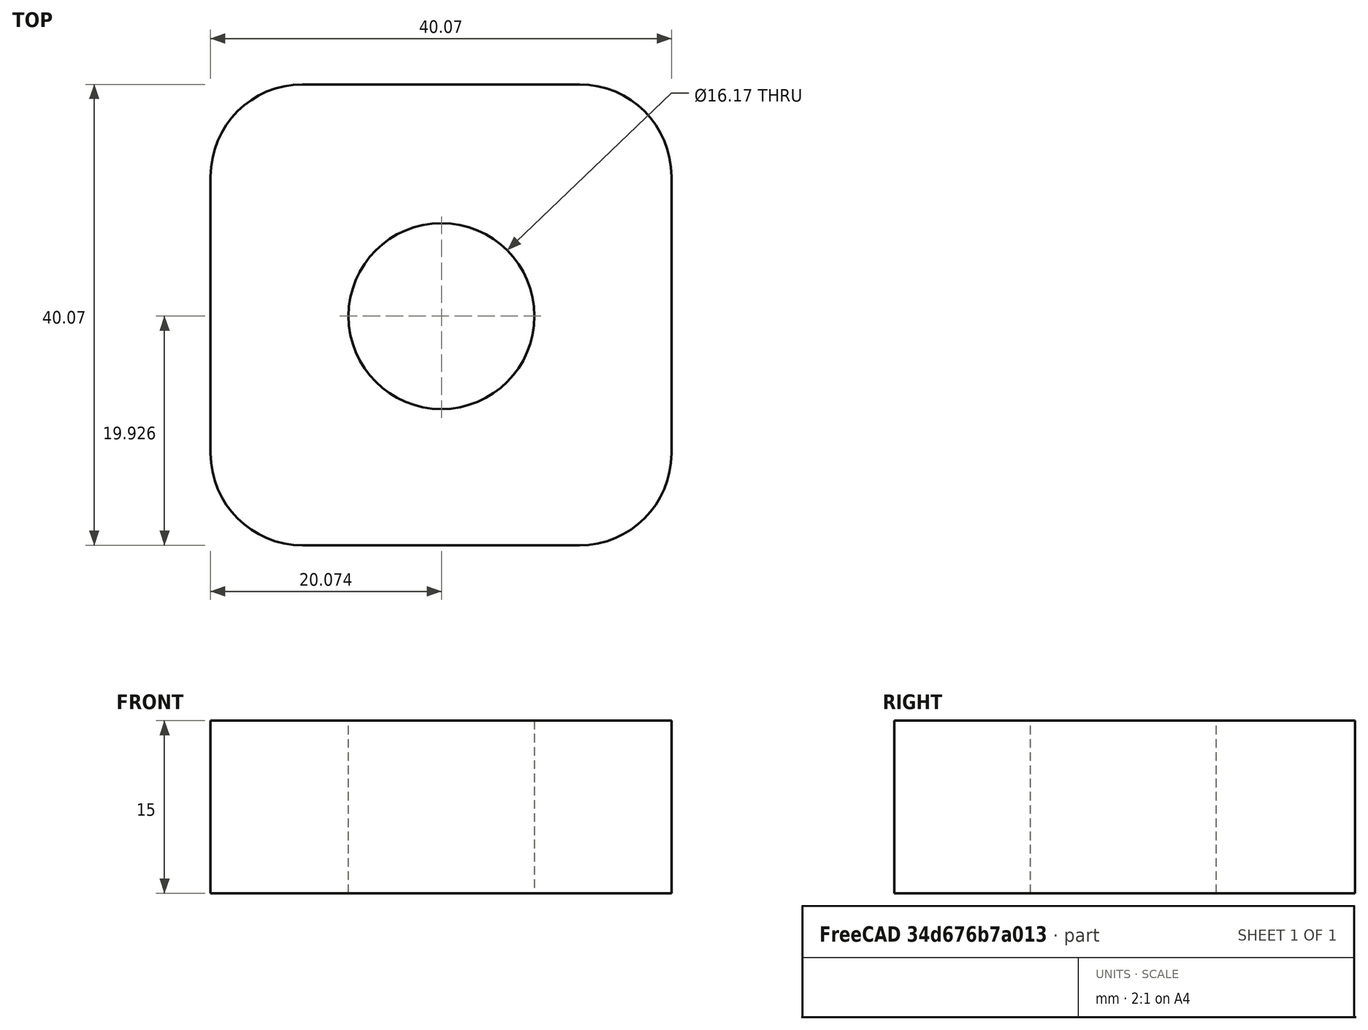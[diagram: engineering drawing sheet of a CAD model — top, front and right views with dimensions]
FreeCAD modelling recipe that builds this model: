
FCSTD DOCUMENT  (FreeCAD 0.21R32552 (Git))
Label: 8x
License: All rights reserved
LicenseURL: http://en.wikipedia.org/wiki/All_rights_reserved
objects: App::FeaturePython×9, App::DocumentObjectGroupPython×4, TechDraw::DrawProjGroupItem×3, TechDraw::DrawViewBalloon×3, Sketcher::SketchObject×2, PartDesign::Pad×1, PartDesign::Pocket×1, PartDesign::Fillet×1, PartDesign::Body×1, TechDraw::DrawSVGTemplate×1, TechDraw::DrawProjGroup×1, TechDraw::DrawPage×1
note: 9 computed .brp shape members not serialized (recipe doc carries the construction recipe); baked Part::Feature solids carry a one-line shape summary decoded from their .brp

FEATURE [Sketcher::SketchObject] Sketch
  FullyConstrained = false
  MapMode = 5
  Support = -> [XY_Plane]
  sketch-geometry (4):
    g0: LineSegment StartX=0 StartY=0 StartZ=0 EndX=40.0741 EndY=0 EndZ=0
    g1: LineSegment StartX=40.0741 StartY=0 StartZ=0 EndX=40.0741 EndY=40.0741 EndZ=0
    g2: LineSegment StartX=40.0741 StartY=40.0741 StartZ=0 EndX=0 EndY=40.0741 EndZ=0
    g3: LineSegment StartX=0 StartY=40.0741 StartZ=0 EndX=0 EndY=0 EndZ=0
  constraints (9):
    c: Coincident(g0,g1)
    c: Coincident(g1,g2)
    c: Coincident(g2,g3)
    c: Coincident(g3,g0)
    c: Horizontal(g0)
    c: Horizontal(g2)
    c: Vertical(g1)
    c: Vertical(g3)
    c: Coincident(g0,g-1)
FEATURE [PartDesign::Pad] Pad
  Direction = (0,0,1)
  Length = 15
  Length2 = 10
  Profile = -> Sketch
  ReferenceAxis = -> Sketch [N_Axis]
  Type = 0
FEATURE [Sketcher::SketchObject] Sketch001
  FullyConstrained = false
  MapMode = 5
  Placement = pos=(0,0,15) rot=(0,0,1;0rad)
  Support = -> [Pad]
  sketch-geometry (1):
    g0: Circle CenterX=20.0741 CenterY=19.9259 CenterZ=0 NormalX=0 NormalY=0 NormalZ=1 AngleXU=0 Radius=8.08325
FEATURE [PartDesign::Pocket] Pocket
  BaseFeature = -> Pad
  Direction = (0,0,-1)
  Length = 5
  Length2 = 5
  Profile = -> Sketch001
  ReferenceAxis = -> Sketch001 [N_Axis]
  Type = 1
FEATURE [PartDesign::Fillet] Fillet
  Base = -> Pocket [Edge2,Edge8,Edge5,Edge1]
  BaseFeature = -> Pocket
  Radius = 8
  SupportTransform = false
  UseAllEdges = false
FEATURE [PartDesign::Body] Body
  Group = -> [Sketch,Pad,Sketch001,Pocket,Fillet]
  Origin = -> Origin
  Tip = -> Fillet
FEATURE [App::FeaturePython] AnnotationPlane  label="AP1"  # WARN: FeaturePython — macro-defined, semantics opaque (R4)
  Direction = (0,1,0)
  Offset = -10
  PointWithOffset = (20.037,30.0741,7.5)
  Type = Unknown
  faces = -> Fillet [Face10]
  p1 = (20.037,40.0741,7.5)
FEATURE [App::FeaturePython] DatumFeature  label="A"  # WARN: FeaturePython — macro-defined, semantics opaque (R4)
  Type = Unknown
FEATURE [App::FeaturePython] DatumSystem  label="DS1: A"  # WARN: FeaturePython — macro-defined, semantics opaque (R4)
  Primary = -> DatumFeature
  Type = Unknown
FEATURE [App::FeaturePython] DatumFeature001  label="B"  # WARN: FeaturePython — macro-defined, semantics opaque (R4)
  Type = Unknown
FEATURE [App::DocumentObjectGroupPython] Annotation2  # scripted group (container) (typed FeaturePython)
  AP = -> AnnotationPlane
  DF = -> DatumFeature001
  Direction = (0,1,0)
  Group = -> [DatumFeature001]
  circumferenceBool = true
  diameter = 0
  faces = -> [Fillet]
  highLimit = 0
  lowLimit = 0
  p1 = (28.1573,19.9259,15)
  selectedPoint = (31.0176,29.9998,17.166)
  spBool = true
  toleranceDiameter = 0
  toleranceSelectBool = true
FEATURE [App::FeaturePython] DatumSystem001  label="DS2: B"  # WARN: FeaturePython — macro-defined, semantics opaque (R4)
  Primary = -> DatumFeature001
  Type = Unknown
FEATURE [App::FeaturePython] AnnotationPlane001  label="AP2"  # WARN: FeaturePython — macro-defined, semantics opaque (R4)
  Direction = (0,0,1)
  Offset = -5
  PointWithOffset = (20.0314,20.054,10)
  Type = Unknown
  faces = -> Fillet [Face5]
  p1 = (20.0314,20.054,15)
FEATURE [App::FeaturePython] GeometricTolerance  label="GT1"  # WARN: FeaturePython — macro-defined, semantics opaque (R4)
  Characteristic = Profile of a surface
  CharacteristicCode = ⌓
  CharacteristicIcon = :/dd/icons/Characteristic/profileOfASurface.svg
  Circumference = false
  DS = -> DatumSystem001
  FeatureControlFrame = Maximum material condition
  FeatureControlFrameCode = Ⓜ
  FeatureControlFrameIcon = :/dd/icons/FeatureControlFrame/maximumMaterialCondition.svg
  ToleranceValue = 0.3
  Type = Unknown
FEATURE [App::DocumentObjectGroupPython] Annotation3  # scripted group (container) (typed FeaturePython)
  AP = -> AnnotationPlane001
  Direction = (0,-1,0)
  GT = -> [GeometricTolerance]
  circumferenceBool = false
  diameter = 0
  faces = -> [Fillet]
  highLimit = 0
  lowLimit = 0
  p1 = (20.037,0,10)
  selectedPoint = (9.03139,-13.946,10)
  spBool = true
  toleranceDiameter = 0
  toleranceSelectBool = true
FEATURE [App::FeaturePython] AnnotationPlane002  label="AP3"  # WARN: FeaturePython — macro-defined, semantics opaque (R4)
  Direction = (0,1,0)
  PointWithOffset = (20.037,40.0741,7.5)
  Type = Unknown
  faces = -> Fillet [Face10]
  p1 = (20.037,40.0741,7.5)
FEATURE [App::FeaturePython] AnnotationPlane003  label="AP4"  # WARN: FeaturePython — macro-defined, semantics opaque (R4)
  Direction = (0,-1,0)
  Offset = -20
  PointWithOffset = (20.037,20,7.5)
  Type = Unknown
  faces = -> Fillet [Face1]
  p1 = (20.037,0,7.5)
FEATURE [App::DocumentObjectGroupPython] Annotation1  # scripted group (container) (typed FeaturePython)
  AP = -> AnnotationPlane003
  DF = -> DatumFeature
  Direction = (0,0,-1)
  Group = -> [DatumFeature]
  circumferenceBool = false
  diameter = 0
  faces = -> [Fillet]
  highLimit = 0
  lowLimit = 0
  p1 = (20.0314,20,0)
  selectedPoint = (22.1323,10.2224,-9.5)
  spBool = true
  toleranceDiameter = 0
  toleranceSelectBool = true
FEATURE [App::DocumentObjectGroupPython] GDT  # scripted group (container) (typed FeaturePython)
  Group = -> [Annotation1,DatumSystem,Annotation2,DatumSystem001,Annotation3,AnnotationPlane002,AnnotationPlane003]
  Type = Unknown
FEATURE [TechDraw::DrawSVGTemplate] Template
  Height = 297
  Orientation = 1
  Template = <path> 0.21/data/Mod/TechDraw/Templates/A3_Landscape_FR_m52.svg
  Width = 420
FEATURE [TechDraw::DrawProjGroupItem] ProjItem  label="Front"
  CoarseView = false
  Direction = (0,0,1)
  Focus = 100
  HardHidden = false
  IsoCount = 0
  IsoHidden = false
  IsoVisible = false
  LockPosition = true
  Perspective = false
  Rotation = 0
  RotationVector = (1,0,0)
  ScaleType = 2
  SeamHidden = false
  SeamVisible = true
  SmoothHidden = false
  SmoothVisible = true
  Source = -> [Fillet]
  Type = 0
  X = 0
  XDirection = (1,0,0)
  Y = 0
FEATURE [TechDraw::DrawProjGroupItem] ProjItem001  label="Left"
  CoarseView = false
  Direction = (-1,0,1e-16)
  Focus = 100
  HardHidden = false
  IsoCount = 0
  IsoHidden = false
  IsoVisible = false
  LockPosition = false
  Perspective = false
  Rotation = 0
  RotationVector = (1,0,0)
  ScaleType = 2
  SeamHidden = false
  SeamVisible = true
  SmoothHidden = false
  SmoothVisible = true
  Source = -> [Fillet]
  Type = 1
  X = 77.537
  XDirection = (1e-16,0,1)
  Y = 0
FEATURE [TechDraw::DrawProjGroupItem] ProjItem002  label="Top"
  CoarseView = false
  Direction = (0,1,0)
  Focus = 100
  HardHidden = false
  IsoCount = 0
  IsoHidden = false
  IsoVisible = false
  LockPosition = false
  Perspective = false
  Rotation = 0
  RotationVector = (1,0,0)
  ScaleType = 2
  SeamHidden = false
  SeamVisible = true
  SmoothHidden = false
  SmoothVisible = true
  Source = -> [Fillet]
  Type = 4
  X = 0
  XDirection = (1,0,0)
  Y = -77.537
FEATURE [TechDraw::DrawProjGroup] ProjGroup
  Anchor = -> ProjItem
  AutoDistribute = true
  LockPosition = false
  ProjectionType = 0
  Rotation = 0
  ScaleType = 0
  Source = -> [Fillet]
  Views = -> [ProjItem,ProjItem001,ProjItem002]
  X = 183.031
  Y = 198.995
  spacingX = 50
  spacingY = 50
FEATURE [TechDraw::DrawViewBalloon] Balloon
  BubbleShape = 6
  EndType = 0
  EndTypeScale = 1
  KinkLength = 5
  LockPosition = false
  OriginX = 0
  OriginY = 20.037
  Rotation = 0
  ScaleType = 0
  ShapeScale = 1
  SourceView = -> ProjItem
  Text = ⌖|⌀0.02|A-A
  TextWrapLen = -1
  X = 63.8379
  Y = 56.8516
FEATURE [TechDraw::DrawViewBalloon] Balloon001
  BubbleShape = 6
  EndType = 0
  EndTypeScale = 1
  KinkLength = 5
  LockPosition = false
  OriginX = 0
  OriginY = 20.037
  Rotation = 0
  ScaleType = 0
  ShapeScale = 1
  SourceView = -> ProjItem001
  Text = ⌓|⌀0,02Ⓜ|AⒸ|B-B
  TextWrapLen = -1
  X = 76.0881
  Y = 38.5532
FEATURE [TechDraw::DrawViewBalloon] Balloon002
  BubbleShape = 5
  EndType = 6
  EndTypeScale = 1
  KinkLength = 0.0001
  LockPosition = false
  OriginX = 7.5
  OriginY = 0
  Rotation = 0
  ScaleType = 0
  ShapeScale = 1
  SourceView = -> ProjItem001
  Text = A
  TextWrapLen = -1
  X = 21.8615
  Y = 0.116906
FEATURE [TechDraw::DrawPage] Page
  KeepUpdated = true
  NextBalloonIndex = 4
  ProjectionType = 0
  Template = -> Template
  Views = -> [ProjGroup,Balloon,Balloon001,Balloon002]
note: 1 file-system path scrubbed to <path> (originals preserved in the JSON sidecar)
